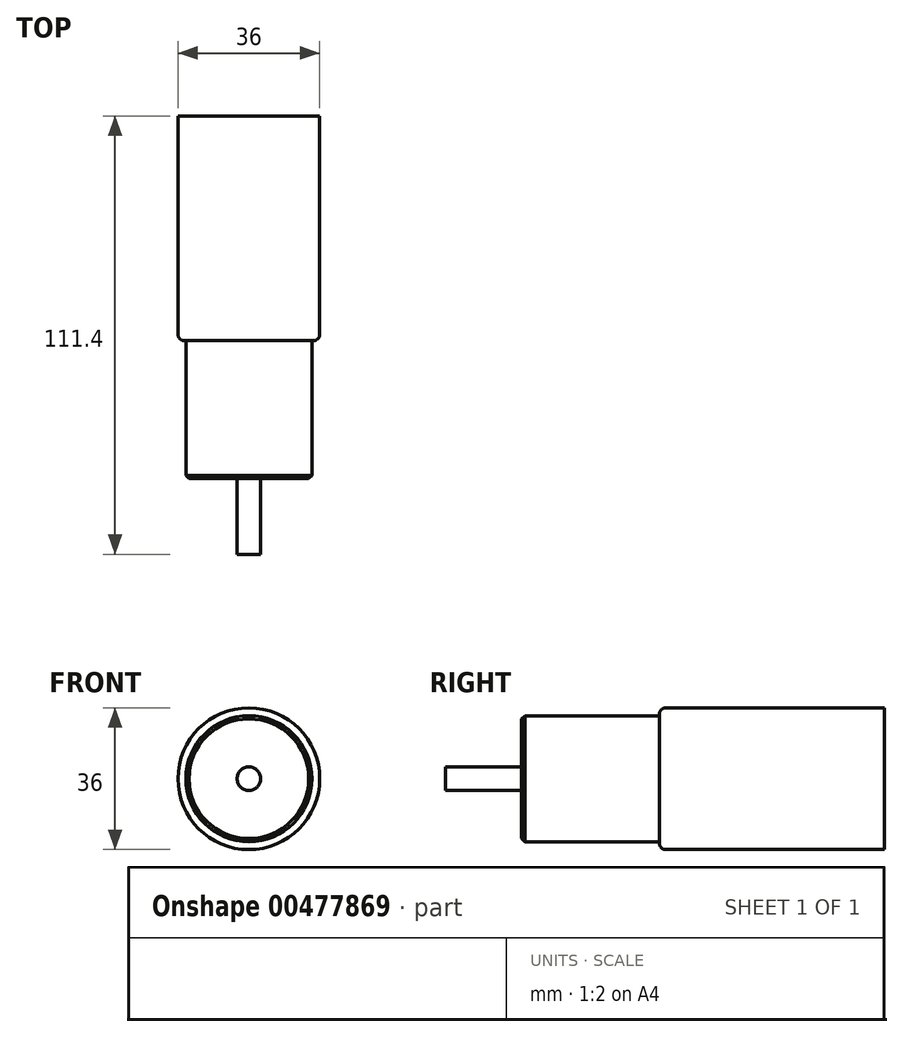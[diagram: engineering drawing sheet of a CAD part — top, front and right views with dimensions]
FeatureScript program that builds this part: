
annotation { "Feature Type Name" : "Feature", "Feature Type Description" : "" }
export const myFeature = defineFeature(function(context is Context, id is Id, definition is map)
    precondition{}
    {
        {
            var Q0;
            Q0=qCreatedBy(makeId("Front.planeOp"),FACE);
            var sketch = newSketch(context, id + "F0", { "sketchPlane" : qUnion([Q0])});
            skCircle(sketch, "E0", {"center": v(0, 0) * mm, "radius": 18 * mm});
            skSolve(sketch);
        }
        {
            var Q0;
            Q0=makeQuery(id+"F0.imprint","IMPRINT",FACE,{"disambiguationData":[TD([[makeQuery(id+"F0.imprint","IMPRINT",EDGE,{"derivedFrom":sQuery(id+"F0.wireOp",EDGE,"E0")}),1.0]])]});
            extrude(context, id + "F1", {"entities" : qUnion([Q0]), "depth" : 57.1 * mm, "offsetDistance" : 25.4 * mm});
        }
        {
            var Q0;
            Q0=makeQuery(id+"F1.opExtrude","CAP_FACE",FACE,{"disambiguationData":[OSD([sQuery(id+"F0.wireOp",EDGE,"E0")])],"isStart":false});
            var sketch = newSketch(context, id + "F2", { "sketchPlane" : qUnion([Q0])});
            skCircle(sketch, "E1", {"center": v(0, 0) * mm, "radius": 16 * mm});
            skSolve(sketch);
        }
        {
            var Q0;
            Q0=makeQuery(id+"F2.imprint","IMPRINT",FACE,{"disambiguationData":[TD([[makeQuery(id+"F2.imprint","IMPRINT",EDGE,{"derivedFrom":sQuery(id+"F2.wireOp",EDGE,"E1")}),1.0]])]});
            extrude(context, id + "F3", {"entities" : qUnion([Q0]), "operationType" : NewBodyOperationType.ADD, "depth" : 35 * mm, "offsetDistance" : 25.4 * mm});
        }
        {
            var Q0;
            Q0=makeQuery(id+"F1.opExtrude","CAP_EDGE",EDGE,{"disambiguationData":[OSD([sQuery(id+"F0.wireOp",EDGE,"E0")])],"isStart":false});
            fillet(context, id + "F4", {"entities" : qUnion([Q0]), "radius" : 1.59 * mm, "tangentPropagation" : true, "allowEdgeOverflow" : false});
        }
        {
            var Q0;
            Q0=makeQuery(id+"F3.opExtrude","CAP_FACE",FACE,{"disambiguationData":[OSD([sQuery(id+"F2.wireOp",EDGE,"E1")])],"isStart":false});
            var sketch = newSketch(context, id + "F5", { "sketchPlane" : qUnion([Q0])});
            skCircle(sketch, "E2", {"center": v(0, 0) * mm, "radius": 3 * mm});
            skSolve(sketch);
        }
        {
            var Q0;
            Q0=makeQuery(id+"F5.imprint","IMPRINT",FACE,{"disambiguationData":[TD([[makeQuery(id+"F5.imprint","IMPRINT",EDGE,{"derivedFrom":sQuery(id+"F5.wireOp",EDGE,"E2")}),1.0]])]});
            extrude(context, id + "F6", {"entities" : qUnion([Q0]), "operationType" : NewBodyOperationType.ADD, "depth" : 19.3 * mm, "offsetDistance" : 25.4 * mm});
        }
        {
            var Q0;
            Q0=makeQuery(id+"F3.opExtrude","CAP_EDGE",EDGE,{"disambiguationData":[OSD([sQuery(id+"F2.wireOp",EDGE,"E1")])],"isStart":false});
            chamfer(context, id + "F7", {"entities" : qUnion([Q0]), "width" : 0.8 * mm, "tangentPropagation" : true});
        }
    });
